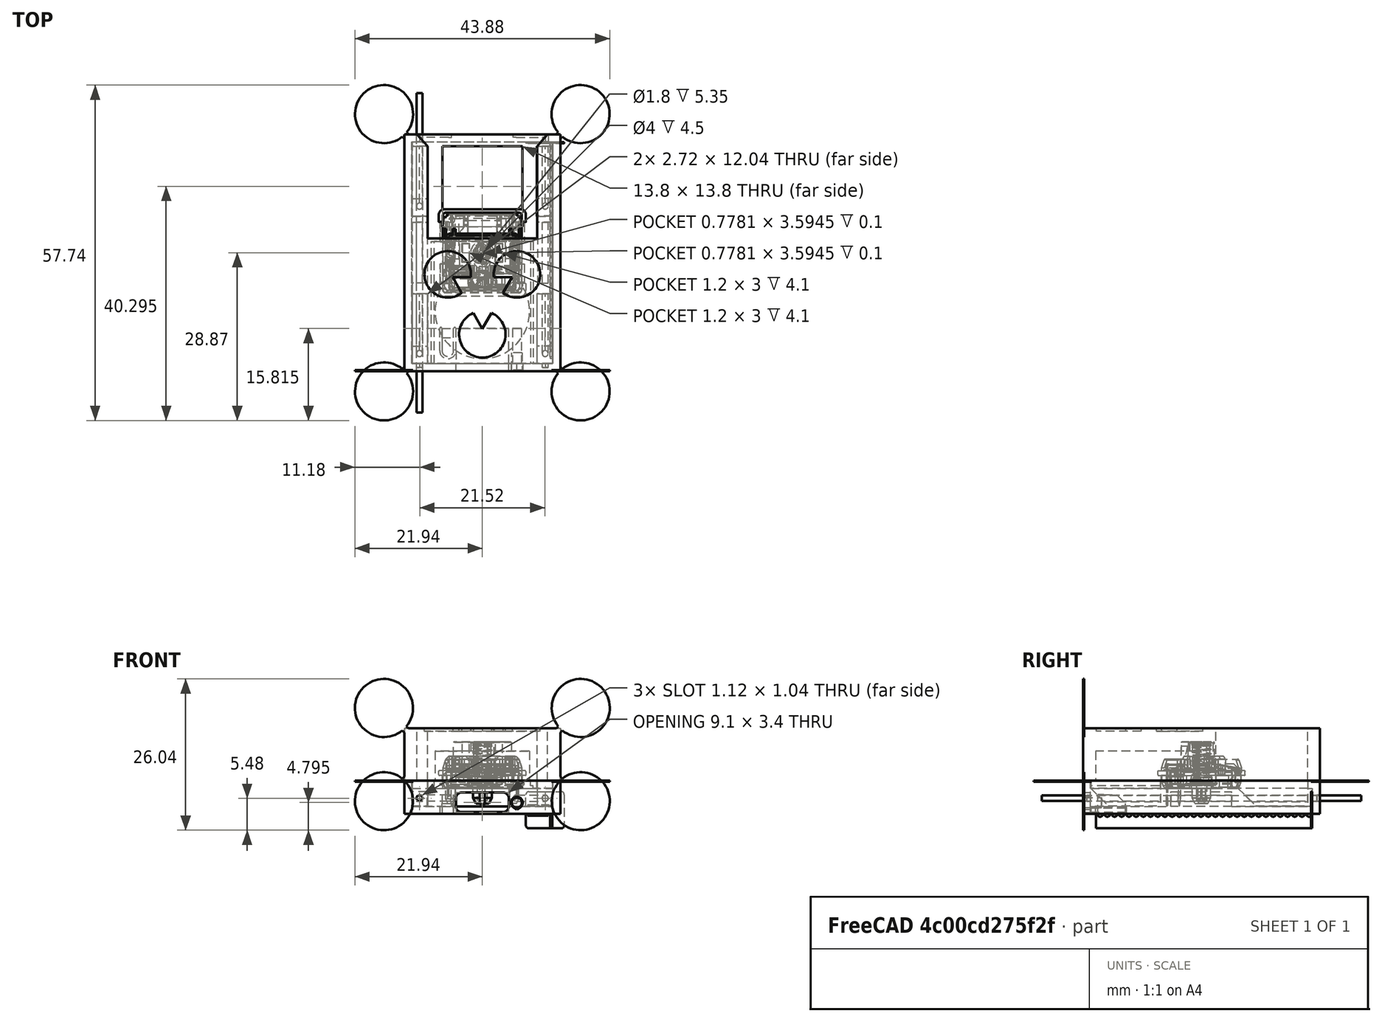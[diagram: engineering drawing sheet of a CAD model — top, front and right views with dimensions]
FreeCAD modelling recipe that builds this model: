
FCSTD DOCUMENT  (FreeCAD 1.1R42788 (Git))
Label: xiao_fit_2
License: All rights reserved
LicenseURL: https://en.wikipedia.org/wiki/All_rights_reserved
objects: Sketcher::SketchObject×31, PartDesign::Pocket×15, PartDesign::Pad×13, Part::Feature×8, App::Point×6, PartDesign::Mirrored×5, PartDesign::Body×5, PartDesign::Hole×3, App::VarSet×2, Mesh::Feature×2, App::Part×1, PartDesign::Chamfer×1, PartDesign::LinearPattern×1
note: 183 computed .brp shape members not serialized (recipe doc carries the construction recipe); baked Part::Feature solids carry a one-line shape summary decoded from their .brp

FEATURE [Sketcher::SketchObject] Sketch
  ArcFitTolerance = 1e-06
  AttachmentSupport = -> [XY_Plane]
  ExternalTypes = [0]
  FullyConstrained = true
  MakeInternals = false
  MapMode = 5
  expr: Constraints[20] = VarSet.ChocHoleWidth
  expr: Constraints[21] = VarSet.ChocHoleHeight
  expr: Constraints[32] = VarSet.XiaoHeight
  expr: Constraints[33] = VarSet.XiaoWidth
  expr: Constraints[34] = VarSet.WallThickness
  expr: Constraints[35] = 2 * VarSet.WallThickness
  expr: Constraints[48] = VarSet.KeycapFrameHorizontal
  expr: Constraints[49] = VarSet.KeycapHorizontalClearance
  expr: Constraints[50] = VarSet.KeycapVerticalClearance
  expr: Constraints[51] = VarSet.KeycapVerticalClearance
  sketch-geometry (20):
    g0: LineSegment StartX=-13.42 StartY=-20.375 StartZ=0 EndX=13.42 EndY=-20.375 EndZ=0
    g1: LineSegment StartX=13.42 StartY=-20.375 StartZ=0 EndX=13.42 EndY=20.375 EndZ=0
    g2: LineSegment StartX=13.42 StartY=20.375 StartZ=0 EndX=-13.42 EndY=20.375 EndZ=0
    g3: LineSegment StartX=-13.42 StartY=20.375 StartZ=0 EndX=-13.42 EndY=-20.375 EndZ=0
    g4: GeomPoint [constr] X=0 Y=0 Z=0
    g5: LineSegment StartX=-6.9 StartY=18.325 StartZ=0 EndX=-6.9 EndY=4.525 EndZ=0
    g6: LineSegment StartX=-6.9 StartY=4.525 StartZ=0 EndX=6.9 EndY=4.525 EndZ=0
    g7: LineSegment StartX=6.9 StartY=4.525 StartZ=0 EndX=6.9 EndY=18.325 EndZ=0
    g8: LineSegment StartX=6.9 StartY=18.325 StartZ=0 EndX=-6.9 EndY=18.325 EndZ=0
    g9: GeomPoint [constr] X=0 Y=11.425 Z=0
    g10: LineSegment StartX=-8.75 StartY=-19.075 StartZ=0 EndX=8.75 EndY=-19.075 EndZ=0
    g11: LineSegment StartX=8.75 StartY=-19.075 StartZ=0 EndX=8.75 EndY=1.925 EndZ=0
    g12: LineSegment StartX=8.75 StartY=1.925 StartZ=0 EndX=-8.75 EndY=1.925 EndZ=0
    g13: LineSegment StartX=-8.75 StartY=1.925 StartZ=0 EndX=-8.75 EndY=-19.075 EndZ=0
    g14: GeomPoint [constr] X=0 Y=-8.575 Z=0
    g15: LineSegment StartX=-13.42 StartY=20.375 StartZ=0 EndX=-9.42 EndY=20.375 EndZ=0
    g16: LineSegment StartX=-9.42 StartY=20.375 StartZ=0 EndX=-9.42 EndY=2.475 EndZ=0
    g17: LineSegment StartX=-9.42 StartY=2.475 StartZ=0 EndX=9.42 EndY=2.475 EndZ=0
    g18: LineSegment StartX=9.42 StartY=2.475 StartZ=0 EndX=9.42 EndY=20.375 EndZ=0
    g19: LineSegment StartX=9.42 StartY=20.375 StartZ=0 EndX=13.42 EndY=20.375 EndZ=0
  constraints (52):
    c: Coincident(g0,g1)
    c: Coincident(g1,g2)
    c: Coincident(g2,g3)
    c: Coincident(g3,g0)
    c: Horizontal(g0)
    c: Horizontal(g2)
    c: Vertical(g1)
    c: Vertical(g3)
    c: Symmetric(g2,g0,g4)
    c: Coincident(g4,g-1)
    c: Coincident(g5,g6)
    c: Coincident(g6,g7)
    c: Coincident(g7,g8)
    c: Coincident(g8,g5)
    c: Vertical(g5)
    c: Vertical(g7)
    c: Horizontal(g6)
    c: Horizontal(g8)
    c: Symmetric(g7,g5,g9)
    c: PointOnObject(g9,g-2)
    c: DistanceX(g8,g8) = 13.8
    c: DistanceY(g7,g7) = 13.8
    c: Coincident(g10,g11)
    c: Coincident(g11,g12)
    c: Coincident(g12,g13)
    c: Coincident(g13,g10)
    c: Horizontal(g10)
    c: Horizontal(g12)
    c: Vertical(g11)
    c: Vertical(g13)
    c: Symmetric(g12,g10,g14)
    c: PointOnObject(g14,g-2)
    c: DistanceY(g11,g11) = 21
    c: DistanceX(g12,g12) = 17.5
    c: DistanceY(g0,g10) = 1.3
    c: DistanceY(g12,g5) = 2.6
    c: Coincident(g2,g15)
    c: PointOnObject(g15,g2)
    c: Coincident(g15,g16)
    c: Vertical(g16)
    c: Coincident(g16,g17)
    c: Horizontal(g17)
    c: Coincident(g17,g18)
    c: PointOnObject(g18,g2)
    c: Vertical(g18)
    c: Coincident(g18,g19)
    c: Coincident(g19,g1)
    c: Equal(g15,g19)
    c: Distance(g19,g19) = 4
    c: DistanceX(g7,g18) = 2.52
    c: DistanceY(g17,g6) = 2.05
    c: DistanceY(g7,g18) = 2.05
FEATURE [App::VarSet] VarSet
  ChocBottomClearance = 5.7
  ChocHoleHeight = 13.8
  ChocHoleWidth = 13.8
  ChocHorizontalSpacing = 5
  ChocVerticalSpacing = 0.2
  Clearance = 0.02
  KeycapFrameHorizontal = 4
  KeycapHorizontalClearance = 2.52
  KeycapVerticalClearance = 2.05
  WallThickness = 1.3
  XiaoHeight = 21
  XiaoThickness = 1.25
  XiaoTopClearance = 0.5
  XiaoWidth = 17.5
  expr: ChocHoleHeight = 13.8 mm
FEATURE [PartDesign::Pad] Pad  label="Base"
  Direction = (0,0,1)
  Length = 1.3
  Length2 = 10
  Profile = -> Sketch [Edge3,Edge9,Edge1,Edge2]
  ReferenceAxis = -> Sketch [N_Axis]
  Refine = true
  Suppressed = false
  Type = 0
  expr: Length = VarSet.WallThickness
FEATURE [Sketcher::SketchObject] Sketch001
  ArcFitTolerance = 1e-06
  AttachmentSupport = -> [Pad]
  ExternalGeometry = -> [Sketch]
  ExternalTypes = [0]
  FullyConstrained = true
  MakeInternals = false
  MapMode = 5
  Placement = pos=(0,0,1.3) rot=(0,0,1;0rad)
  sketch-geometry (4):
    g0: LineSegment StartX=-6.9 StartY=18.325 StartZ=0 EndX=-6.9 EndY=4.525 EndZ=0
    g1: LineSegment StartX=-6.9 StartY=4.525 StartZ=0 EndX=6.9 EndY=4.525 EndZ=0
    g2: LineSegment StartX=6.9 StartY=4.525 StartZ=0 EndX=6.9 EndY=18.325 EndZ=0
    g3: LineSegment StartX=6.9 StartY=18.325 StartZ=0 EndX=-6.9 EndY=18.325 EndZ=0
  constraints (10):
    c: Coincident(g0,g1)
    c: Coincident(g1,g2)
    c: Coincident(g2,g3)
    c: Coincident(g3,g0)
    c: Vertical(g0)
    c: Vertical(g2)
    c: Horizontal(g1)
    c: Horizontal(g3)
    c: Coincident(g0,g-3)
    c: Coincident(g1,g-4)
FEATURE [PartDesign::Pocket] Pocket  label="ChocHole"
  BaseFeature = -> Pad
  Direction = (0,0,-1)
  Length = 5
  Length2 = 5
  Profile = -> Sketch001
  ReferenceAxis = -> Sketch001 [N_Axis]
  Refine = true
  Suppressed = false
  Type = 1
FEATURE [Mesh::Feature] MBK_Keycap___1u  label="MBK_Keycap_-_1u"
  Placement = pos=(0,0,6.61) rot=(0,0,1;0rad)
FEATURE [Part::Feature] Part__Feature  label="bottom_stabilizer"
  shape: bbox 15.16 x 15.16 x 5.85 mm, 308 faces (baked)
FEATURE [Part::Feature] Part__Feature001  label="contact"
  Placement = pos=(0,-5.9,0) rot=(0,0,1;0rad)
  shape: bbox 1.2 x 2.241 x 2.141 mm, 33 faces (baked)
FEATURE [Part::Feature] Part__Feature002  label="pin1"
  Placement = pos=(0,-5.9,0) rot=(0,0,1;0rad)
  shape: bbox 9.72 x 2.05 x 7 mm, 141 faces (baked)
FEATURE [Part::Feature] Part__Feature003  label="pin2"
  Placement = pos=(-5,-3.8,0) rot=(0,0,1;0rad)
  shape: bbox 3.2 x 0.65 x 7 mm, 30 faces (baked)
FEATURE [Part::Feature] Part__Feature004  label="top_stabilizer"
  Placement = pos=(0,0,3) rot=(0,0,1;0rad)
  shape: bbox 14.5 x 13.8 x 7.5 mm, 348 faces (baked)
FEATURE [Part::Feature] Part__Feature005  label="stabilizer"
  Placement = pos=(0,6.25,3) rot=(-1,0,0;0.20944rad)
  shape: bbox 9.432 x 7.756 x 2.155 mm, 7 faces (baked)
FEATURE [Part::Feature] Part__Feature006  label="stem_stabilizer"
  Placement = pos=(0,0,3.3) rot=(0,0,1;0rad)
  shape: bbox 11.5 x 5.7 x 7 mm, 99 faces (baked)
FEATURE [Part::Feature] Part__Feature007  label="shrunken_spring"
  Placement = pos=(0,0,4.15) rot=(0,0,1;0rad)
  shape: bbox 3.3 x 3.3 x 7.484 mm, 14 faces (baked)
FEATURE [App::Part] red  label="Choc"
  Group = -> [Part__Feature,Part__Feature001,Part__Feature002,Part__Feature003,Part__Feature004,Part__Feature005,Part__Feature006,Part__Feature007,MBK_Keycap___1u]
  Origin = -> Origin001
  Placement = pos=(0.08,11.69,-0.89) rot=(0,0,1;0rad)
  expr: .Placement.Base.z = 0
FEATURE [Mesh::Feature] SeeedXiao_01  label="SeeedXiao-01"
  Placement = pos=(-8.89,-20.59,0.4) rot=(0.707107,0.707107,0;3.14159rad)
FEATURE [Sketcher::SketchObject] Sketch002
  ArcFitTolerance = 1e-06
  AttachmentSupport = -> [Pocket]
  ExternalGeometry = -> [Pocket]
  ExternalTypes = [0]
  FullyConstrained = true
  MakeInternals = false
  MapMode = 5
  Placement = pos=(0,0,0) rot=(1,0,0;3.14159rad)
  expr: Constraints[18] = VarSet.WallThickness
  expr: Constraints[19] = VarSet.WallThickness
  expr: Constraints[20] = VarSet.WallThickness
  expr: Constraints[21] = VarSet.WallThickness
  sketch-geometry (8):
    g0: LineSegment StartX=-13.42 StartY=20.375 StartZ=0 EndX=-13.42 EndY=-20.375 EndZ=0
    g1: LineSegment StartX=-13.42 StartY=-20.375 StartZ=0 EndX=13.42 EndY=-20.375 EndZ=0
    g2: LineSegment StartX=13.42 StartY=-20.375 StartZ=0 EndX=13.42 EndY=20.375 EndZ=0
    g3: LineSegment StartX=13.42 StartY=20.375 StartZ=0 EndX=-13.42 EndY=20.375 EndZ=0
    g4: LineSegment StartX=-12.12 StartY=19.075 StartZ=0 EndX=-12.12 EndY=-19.075 EndZ=0
    g5: LineSegment StartX=-12.12 StartY=-19.075 StartZ=0 EndX=12.12 EndY=-19.075 EndZ=0
    g6: LineSegment StartX=12.12 StartY=-19.075 StartZ=0 EndX=12.12 EndY=19.075 EndZ=0
    g7: LineSegment StartX=12.12 StartY=19.075 StartZ=0 EndX=-12.12 EndY=19.075 EndZ=0
  constraints (22):
    c: Coincident(g0,g1)
    c: Coincident(g1,g2)
    c: Coincident(g2,g3)
    c: Coincident(g3,g0)
    c: Vertical(g0)
    c: Vertical(g2)
    c: Horizontal(g1)
    c: Horizontal(g3)
    c: Coincident(g0,g-3)
    c: Coincident(g1,g-4)
    c: Coincident(g4,g5)
    c: Coincident(g5,g6)
    c: Coincident(g6,g7)
    c: Coincident(g7,g4)
    c: Vertical(g4)
    c: Vertical(g6)
    c: Horizontal(g5)
    c: Horizontal(g7)
    c: DistanceX(g6,g2) = 1.3
    c: DistanceX(g0,g4) = 1.3
    c: DistanceY(g6,g2) = 1.3
    c: DistanceY(g1,g5) = 1.3
FEATURE [PartDesign::Pad] Pad001  label="Walls"
  BaseFeature = -> Pocket
  Direction = (0,0,-1)
  Length = 4.4
  Length2 = 10
  Profile = -> Sketch002
  ReferenceAxis = -> Sketch002 [N_Axis]
  Refine = true
  Suppressed = false
  Type = 0
  expr: Length = VarSet.ChocBottomClearance - VarSet.WallThickness
FEATURE [Sketcher::SketchObject] Sketch003
  ArcFitTolerance = 1e-06
  AttachmentSupport = -> [Pad001]
  ExternalGeometry = -> [Sketch]
  ExternalTypes = [0]
  FullyConstrained = true
  MakeInternals = false
  MapMode = 5
  Placement = pos=(0,0,0) rot=(1,0,0;3.14159rad)
  expr: Constraints[5] = VarSet.Clearance
  expr: Constraints[7] = VarSet.Clearance
  expr: Constraints[8] = VarSet.Clearance
  sketch-geometry (4):
    g0: LineSegment StartX=-8.77 StartY=19.075 StartZ=0 EndX=-8.77 EndY=-1.945 EndZ=0
    g1: LineSegment StartX=-8.77 StartY=-1.945 StartZ=0 EndX=8.77 EndY=-1.945 EndZ=0
    g2: LineSegment StartX=8.77 StartY=-1.945 StartZ=0 EndX=8.77 EndY=19.075 EndZ=0
    g3: LineSegment StartX=8.77 StartY=19.075 StartZ=0 EndX=-8.77 EndY=19.075 EndZ=0
  constraints (12):
    c: Coincident(g0,g1)
    c: Coincident(g1,g2)
    c: Vertical(g0)
    c: Vertical(g2)
    c: Horizontal(g1)
    c: DistanceX(g0,g-3) = 0.02
    c: Horizontal(g2,g-4)
    c: DistanceX(g-4,g2) = 0.02
    c: DistanceY(g1,g-4) = 0.02
    c: Coincident(g3,g2)
    c: Coincident(g3,g0)
    c: Horizontal(g3)
FEATURE [PartDesign::Pocket] Pocket001  label="XiaoHole"
  BaseFeature = -> Pad001
  Direction = (0,0,1)
  Length = 0.4
  Length2 = 5
  Profile = -> Sketch003
  ReferenceAxis = -> Sketch003 [N_Axis]
  Refine = true
  Suppressed = false
  Type = 0
FEATURE [Sketcher::SketchObject] Sketch004
  ArcFitTolerance = 1e-06
  AttachmentSupport = -> [Pocket001]
  ExternalGeometry = -> [Pocket001]
  ExternalTypes = [0]
  FullyConstrained = true
  MakeInternals = false
  MapMode = 5
  Placement = pos=(0,0,0.4) rot=(1,0,0;3.14159rad)
  sketch-geometry (4):
    g0: LineSegment StartX=-8.27 StartY=19.075 StartZ=0 EndX=-8.27 EndY=-1.945 EndZ=0
    g1: LineSegment StartX=-8.27 StartY=-1.945 StartZ=0 EndX=8.27 EndY=-1.945 EndZ=0
    g2: LineSegment StartX=8.27 StartY=-1.945 StartZ=0 EndX=8.27 EndY=19.075 EndZ=0
    g3: LineSegment StartX=8.27 StartY=19.075 StartZ=0 EndX=-8.27 EndY=19.075 EndZ=0
  constraints (12):
    c: Coincident(g0,g1)
    c: Coincident(g1,g2)
    c: Coincident(g2,g3)
    c: Coincident(g3,g0)
    c: Vertical(g0)
    c: Vertical(g2)
    c: Horizontal(g1)
    c: Horizontal(g3)
    c: PointOnObject(g0,g-5)
    c: PointOnObject(g1,g-6)
    c: DistanceX(g1,g-6) = 0.5
    c: DistanceX(g-6,g0) = 0.5
FEATURE [PartDesign::Pocket] Pocket002  label="XiaoHolder"
  BaseFeature = -> Pocket001
  Direction = (0,0,1)
  Length = 5
  Length2 = 5
  Profile = -> Sketch004
  ReferenceAxis = -> Sketch004 [N_Axis]
  Refine = true
  Suppressed = false
  Type = 0
FEATURE [Sketcher::SketchObject] Sketch005
  ArcFitTolerance = 1e-06
  AttachmentSupport = -> [Pocket002]
  ExternalGeometry = -> [Pocket002]
  ExternalTypes = [0]
  FullyConstrained = true
  MakeInternals = false
  MapMode = 5
  Placement = pos=(0,-20.375,1.2e-14) rot=(1,0,0;1.5708rad)
  sketch-geometry (13):
    g0: LineSegment StartX=-3.55 StartY=-4.125 StartZ=0 EndX=3.55 EndY=-4.125 EndZ=0
    g1: LineSegment StartX=4.55 StartY=-3.125 StartZ=0 EndX=4.55 EndY=-1.725 EndZ=0
    g2: LineSegment StartX=3.55 StartY=-0.725 StartZ=0 EndX=-3.55 EndY=-0.725 EndZ=0
    g3: LineSegment StartX=-4.55 StartY=-1.725 StartZ=0 EndX=-4.55 EndY=-3.125 EndZ=0
    g4: ArcOfCircle CenterX=-3.55 CenterY=-3.125 CenterZ=0 NormalX=0 NormalY=0 NormalZ=1 AngleXU=0 Radius=1 StartAngle=3.14159 EndAngle=4.71239
    g5: ArcOfCircle CenterX=3.55 CenterY=-3.125 CenterZ=0 NormalX=0 NormalY=0 NormalZ=1 AngleXU=0 Radius=1 StartAngle=4.71239 EndAngle=6.28319
    g6: ArcOfCircle CenterX=3.55 CenterY=-1.725 CenterZ=0 NormalX=0 NormalY=0 NormalZ=1 AngleXU=0 Radius=1 StartAngle=0 EndAngle=1.5708
    g7: ArcOfCircle CenterX=-3.55 CenterY=-1.725 CenterZ=0 NormalX=0 NormalY=0 NormalZ=1 AngleXU=0 Radius=1 StartAngle=1.5708 EndAngle=3.14159
    g8: GeomPoint [constr] X=-4.55 Y=-4.125 Z=0
    g9: GeomPoint [constr] X=4.55 Y=-0.725 Z=0
    g10: ArcOfCircle CenterX=5.95 CenterY=-2.475 CenterZ=0 NormalX=0 NormalY=0 NormalZ=1 AngleXU=0 Radius=1 StartAngle=5.23599 EndAngle=10.472
    g11: LineSegment StartX=5.95 StartY=-3.6297 StartZ=0 EndX=5.45 EndY=-3.34103 EndZ=0
    g12: LineSegment StartX=5.95 StartY=-3.6297 StartZ=0 EndX=6.45 EndY=-3.34103 EndZ=0
  constraints (31):
    c: Tangent(g0,g4) = -1.5708
    c: Tangent(g0,g5) = -1.5708
    c: Tangent(g1,g5) = -1.5708
    c: Tangent(g1,g6) = -1.5708
    c: Tangent(g2,g6) = -1.5708
    c: Tangent(g2,g7) = -1.5708
    c: Tangent(g3,g7) = -1.5708
    c: Tangent(g3,g4) = -1.5708
    c: Horizontal(g0)
    c: Vertical(g1)
    c: Vertical(g3)
    c: Equal(g4,g5)
    c: Equal(g5,g6)
    c: Equal(g6,g7)
    c: PointOnObject(g8,g0)
    c: PointOnObject(g8,g3)
    c: PointOnObject(g9,g1)
    c: PointOnObject(g9,g2)
    c: Radius(g5) = 1
    c: DistanceX(g3,g1) = 9.1
    c: DistanceY(g0,g2) = 3.4
    c: Symmetric(g2,g2,g-2)
    c: DistanceY(g2,g-4) = 1.125
    c: DistanceX(g1,g10) = 1.4
    c: DistanceY(g10,g1) = 0.75
    c: Coincident(g12,g11)
    c: Angle(g12,g11) = 2.0944
    c: Horizontal(g12,g11)
    c: Diameter(g10) = 2
    c: Tangent(g11,g10) = 1.5708
    c: Tangent(g12,g10) = -1.5708
FEATURE [PartDesign::Pocket] Pocket003  label="USB-Hole"
  BaseFeature = -> Pocket002
  Direction = (0,1,-2e-16)
  Length = 5
  Length2 = 5
  Profile = -> Sketch005
  ReferenceAxis = -> Sketch005 [N_Axis]
  Refine = true
  Suppressed = false
  Type = 2
FEATURE [App::Point] Origin004  label="Origin"
  Role = Origin
FEATURE [App::Point] Origin005  label="Origin"
  Role = Origin
FEATURE [Sketcher::SketchObject] Sketch010
  ArcFitTolerance = 1e-06
  AttachmentSupport = -> [Pad001]
  ExternalGeometry = -> [Pocket003]
  ExternalTypes = [0,0,0]
  FullyConstrained = true
  MakeInternals = false
  MapMode = 5
  Placement = pos=(0,20.375,-1.2e-14) rot=(0,0.707107,0.707107;3.14159rad)
  sketch-geometry (1):
    g0: Circle CenterX=-10.82 CenterY=-1.7 CenterZ=0 NormalX=0 NormalY=0 NormalZ=1 AngleXU=0 Radius=0.5
  constraints (3):
    c: Diameter(g0) = 1
    c: DistanceY(g-4,g0) = 2.7
    c: DistanceX(g-4,g0) = 1.3
FEATURE [PartDesign::Hole] Hole  label="PinHole"
  BaseFeature = -> Pocket003
  BaseProfileType = 7
  CustomThreadClearance = 0
  Depth = 5
  DepthType = 0
  Diameter = 1.04
  DrillForDepth = false
  DrillPoint = 1
  DrillPointAngle = 118
  HoleCutCountersinkAngle = 90
  HoleCutCustomValues = false
  HoleCutDepth = 0
  HoleCutDiameter = 0
  HoleCutType = 0
  ModelThread = false
  Profile = -> Sketch010
  Refine = true
  Suppressed = false
  Tapered = false
  TaperedAngle = 90
  TeardropAngle = 120
  TeardropRotation = 270
  ThreadClass = 0
  ThreadDepth = 5
  ThreadDepthType = 0
  ThreadDiameter = 1.04
  ThreadDirection = 0
  ThreadFit = 0
  ThreadSize = 0
  ThreadType = 0
  Threaded = false
  UseCustomThreadClearance = false
  expr: Diameter = 1 mm + 2 * VarSet.Clearance
FEATURE [Sketcher::SketchObject] Sketch010_Teardrops
  ArcFitTolerance = 1e-06
  AttachmentSupport = -> [Sketch010]
  ExternalTypes = [0]
  FullyConstrained = true
  MakeInternals = false
  MapMode = 2
  Placement = pos=(0,20.375,-1.2e-14) rot=(0,0.707107,0.707107;3.14159rad)
  expr: Constraints[5] = Sketch010.Geometry[0].Center.x * 1 mm
  expr: Constraints[6] = Sketch010.Geometry[0].Center.y * 1 mm
  expr: Constraints[7] = Hole.Diameter
  expr: Constraints[8] = Hole.TeardropAngle
  expr: Constraints[9] = Hole.TeardropRotation
  sketch-geometry (4):
    g0: ArcOfCircle CenterX=-10.82 CenterY=-1.7 CenterZ=0 NormalX=0 NormalY=0 NormalZ=1 AngleXU=0 Radius=0.52 StartAngle=5.23599 EndAngle=10.472
    g1: LineSegment StartX=-10.56 StartY=-2.15033 StartZ=0 EndX=-10.82 EndY=-2.30044 EndZ=0
    g2: LineSegment StartX=-11.08 StartY=-2.15033 StartZ=0 EndX=-10.82 EndY=-2.30044 EndZ=0
    g3: LineSegment [constr] StartX=-10.82 StartY=-1.7 StartZ=0 EndX=-10.82 EndY=-2.30044 EndZ=0
  constraints (10):
    c: Coincident(g1,g2)
    c: Coincident(g1,g3)
    c: Coincident(g0,g3)
    c: Tangent(g0,g1) = 1.5708
    c: Tangent(g0,g2) = -1.5708
    c: DistanceX(g0) = -10.82
    c: DistanceY(g0) = -1.7
    c: Diameter(g0) = 1.04
    c: Angle(g1,g2) = 2.0944
    c: Angle(g3) = 4.71239
FEATURE [PartDesign::Pocket] Hole_Teardrops  label="PinHole_Teardrops"
  BaseFeature = -> Hole
  Direction = (0,-1,2e-16)
  Length = 5
  Length2 = 5
  Profile = -> Sketch010_Teardrops
  ReferenceAxis = -> Sketch010_Teardrops [N_Axis]
  Refine = true
  Suppressed = false
  Type = 0
  expr: Length = Hole.Depth
  expr: Type = Hole.DepthType
FEATURE [App::Point] Origin008
  Role = Origin
FEATURE [Sketcher::SketchObject] Sketch016
  ArcFitTolerance = 1e-06
  AttachmentSupport = -> [Origin007]
  ExternalTypes = [0]
  FullyConstrained = true
  MakeInternals = false
  MapMode = 5
  expr: Constraints[6] = VarSet.ChocHoleWidth + 2 * VarSet.KeycapHorizontalClearance + 2 * VarSet.KeycapFrameHorizontal - 2 * VarSet.WallThickness - 2 * VarSet.Clearance
  expr: Constraints[8] = VarSet.KeycapVerticalClearance + VarSet.ChocHoleHeight + VarSet.WallThickness + VarSet.XiaoHeight - 2 * VarSet.Clearance
  sketch-geometry (4):
    g0: LineSegment StartX=-12.1 StartY=19.055 StartZ=0 EndX=-12.1 EndY=-19.055 EndZ=0
    g1: LineSegment StartX=-12.1 StartY=-19.055 StartZ=0 EndX=12.1 EndY=-19.055 EndZ=0
    g2: LineSegment StartX=12.1 StartY=-19.055 StartZ=0 EndX=12.1 EndY=19.055 EndZ=0
    g3: LineSegment StartX=12.1 StartY=19.055 StartZ=0 EndX=-12.1 EndY=19.055 EndZ=0
  constraints (10):
    c: Coincident(g0,g1)
    c: Coincident(g1,g2)
    c: Coincident(g2,g3)
    c: Coincident(g3,g0)
    c: Vertical(g0)
    c: Horizontal(g1)
    c: DistanceX(g3,g3) = 24.2
    c: Symmetric(g2,g0,g-2)
    c: DistanceY(g2,g2) = 38.11
    c: Symmetric(g2,g1,g-1)
FEATURE [PartDesign::Pad] Pad004  label="Body001"
  Direction = (0,0,1)
  Length = 1.3
  Length2 = 10
  Profile = -> Sketch016
  ReferenceAxis = -> Sketch016 [N_Axis]
  Refine = true
  Suppressed = false
  Type = 0
  expr: Length = VarSet.WallThickness
FEATURE [Sketcher::SketchObject] Sketch017
  ArcFitTolerance = 1e-06
  AttachmentSupport = -> [Pad004]
  ExternalTypes = [0]
  FullyConstrained = false
  MakeInternals = false
  MapMode = 5
  Placement = pos=(0,-19.055,0) rot=(1,0,0;1.5708rad)
  sketch-geometry (11):
    g0: LineSegment StartX=-4.55 StartY=2.69281 StartZ=0 EndX=-4.55 EndY=1.29281 EndZ=0
    g1: LineSegment StartX=-3.55 StartY=0.292812 StartZ=0 EndX=3.55 EndY=0.292812 EndZ=0
    g2: LineSegment StartX=4.55 StartY=1.29281 StartZ=0 EndX=4.55 EndY=2.69281 EndZ=0
    g3: LineSegment StartX=3.55 StartY=3.69281 StartZ=0 EndX=-3.55 EndY=3.69281 EndZ=0
    g4: ArcOfCircle CenterX=-3.55 CenterY=2.69281 CenterZ=0 NormalX=0 NormalY=0 NormalZ=1 AngleXU=0 Radius=1 StartAngle=1.5708 EndAngle=3.14159
    g5: ArcOfCircle CenterX=-3.55 CenterY=1.29281 CenterZ=0 NormalX=0 NormalY=0 NormalZ=1 AngleXU=0 Radius=1 StartAngle=3.14159 EndAngle=4.71239
    g6: ArcOfCircle CenterX=3.55 CenterY=1.29281 CenterZ=0 NormalX=0 NormalY=0 NormalZ=1 AngleXU=0 Radius=1 StartAngle=4.71239 EndAngle=6.28319
    g7: ArcOfCircle CenterX=3.55 CenterY=2.69281 CenterZ=0 NormalX=0 NormalY=0 NormalZ=1 AngleXU=0 Radius=1 StartAngle=0 EndAngle=1.5708
    g8: GeomPoint [constr] X=-4.55 Y=3.69281 Z=0
    g9: GeomPoint [constr] X=4.55 Y=0.292812 Z=0
    g10: Circle CenterX=5.95 CenterY=1.94281 CenterZ=0 NormalX=0 NormalY=0 NormalZ=1 AngleXU=0 Radius=1
  constraints (25):
    c: Tangent(g0,g4) = -1.5708
    c: Tangent(g0,g5) = -1.5708
    c: Tangent(g1,g5) = -1.5708
    c: Tangent(g1,g6) = -1.5708
    c: Tangent(g2,g6) = -1.5708
    c: Tangent(g2,g7) = -1.5708
    c: Tangent(g3,g7) = -1.5708
    c: Tangent(g3,g4) = -1.5708
    c: Vertical(g0)
    c: Vertical(g2)
    c: Horizontal(g1)
    c: Equal(g4,g5)
    c: Equal(g5,g6)
    c: Equal(g6,g7)
    c: PointOnObject(g8,g0)
    c: PointOnObject(g8,g3)
    c: PointOnObject(g9,g1)
    c: PointOnObject(g9,g2)
    c: Radius(g5) = 1
    c: DistanceX(g0,g2) = 9.1
    c: DistanceY(g1,g3) = 3.4
    c: Symmetric(g3,g3,g-2)
    c: DistanceX(g2,g10) = 1.4
    c: Diameter(g10) = 2
    c: DistanceY(g10,g2) = 0.75
FEATURE [PartDesign::Pocket] Pocket007  label="USB-Hole001"
  BaseFeature = -> Pad004
  Direction = (0,1,-2e-16)
  Length = 6
  Length2 = 5
  Profile = -> Sketch017
  ReferenceAxis = -> Sketch017 [N_Axis]
  Refine = true
  Suppressed = false
  Type = 0
FEATURE [Sketcher::SketchObject] Sketch018
  ArcFitTolerance = 1e-06
  AttachmentSupport = -> [Pocket007]
  ExternalGeometry = -> [Pocket007]
  ExternalTypes = [0,0]
  FullyConstrained = false
  MakeInternals = false
  MapMode = 5
  Placement = pos=(0,0,1.3) rot=(0,0,1;0rad)
  sketch-geometry (8):
    g0: LineSegment StartX=-4.55 StartY=-13.055 StartZ=0 EndX=-4.55 EndY=-16.8372 EndZ=0
    g1: LineSegment StartX=-7.35 StartY=-16.8372 StartZ=0 EndX=-7.35 EndY=-13.055 EndZ=0
    g2: ArcOfCircle CenterX=-7.15 CenterY=-13.055 CenterZ=0 NormalX=0 NormalY=0 NormalZ=1 AngleXU=0 Radius=0.2 StartAngle=2.5e-15 EndAngle=3.14159
    g3: LineSegment StartX=-6.95 StartY=-13.055 StartZ=0 EndX=-6.95 EndY=-16.8372 EndZ=0
    g4: LineSegment StartX=-4.95 StartY=-16.8372 StartZ=0 EndX=-4.95 EndY=-13.055 EndZ=0
    g5: ArcOfCircle CenterX=-4.75 CenterY=-13.055 CenterZ=0 NormalX=0 NormalY=0 NormalZ=1 AngleXU=0 Radius=0.2 StartAngle=3.6269e-08 EndAngle=3.14159
    g6: ArcOfCircle CenterX=-5.95 CenterY=-16.8372 CenterZ=0 NormalX=0 NormalY=0 NormalZ=1 AngleXU=0 Radius=1 StartAngle=3.14159 EndAngle=6.28319
    g7: ArcOfCircle CenterX=-5.95 CenterY=-16.8372 CenterZ=0 NormalX=0 NormalY=0 NormalZ=1 AngleXU=0 Radius=1.4 StartAngle=3.14159 EndAngle=6.28319
  constraints (18):
    c: Vertical(g0)
    c: Vertical(g1)
    c: Tangent(g1,g2) = 1.5708
    c: Tangent(g2,g3) = 1.5708
    c: Tangent(g4,g5) = 1.5708
    c: Coincident(g5,g0)
    c: Equal(g5,g2)
    c: Radius(g5) = 0.2
    c: Vertical(g3)
    c: Vertical(g4)
    c: Equal(g3,g4)
    c: Coincident(g7,g6)
    c: Tangent(g6,g4) = -1.5708
    c: Tangent(g6,g3) = -1.5708
    c: DistanceX(g2,g4) = 2
    c: Coincident(g0,g-3)
    c: Tangent(g7,g1) = 1.5708
    c: Tangent(g7,g0) = 1.5708
FEATURE [Sketcher::SketchObject] Sketch019
  ArcFitTolerance = 1e-06
  AttachmentSupport = -> [Pad004]
  ExternalGeometry = -> [Pad004]
  ExternalTypes = [0]
  FullyConstrained = false
  MakeInternals = false
  MapMode = 5
  Placement = pos=(0,0,1.3) rot=(0,0,1;0rad)
  sketch-geometry (4):
    g0: LineSegment StartX=12.1 StartY=5.24157 StartZ=0 EndX=9.5 EndY=5.24157 EndZ=0
    g1: LineSegment StartX=9.5 StartY=5.24157 StartZ=0 EndX=9.5 EndY=-5.24157 EndZ=0
    g2: LineSegment StartX=9.5 StartY=-5.24157 StartZ=0 EndX=12.1 EndY=-5.24157 EndZ=0
    g3: LineSegment StartX=12.1 StartY=-5.24157 StartZ=0 EndX=12.1 EndY=5.24157 EndZ=0
  constraints (10):
    c: Coincident(g0,g1)
    c: Coincident(g1,g2)
    c: Coincident(g2,g3)
    c: Coincident(g3,g0)
    c: Horizontal(g0)
    c: Horizontal(g2)
    c: Vertical(g3)
    c: Symmetric(g0,g1,g-1)
    c: DistanceX(g0,g0) = 2.6
    c: PointOnObject(g0,g-3)
FEATURE [PartDesign::Pad] Pad005  label="Holder"
  BaseFeature = -> Pocket007
  Direction = (0,0,1)
  Length = 2.5
  Length2 = 10
  Profile = -> Sketch019
  ReferenceAxis = -> Sketch019 [N_Axis]
  Refine = true
  Suppressed = false
  Type = 0
FEATURE [Sketcher::SketchObject] Sketch020
  ArcFitTolerance = 1e-06
  AttachmentSupport = -> [Pad005]
  ExternalGeometry = -> [Pad005]
  ExternalTypes = [0,0]
  FullyConstrained = true
  MakeInternals = false
  MapMode = 5
  Placement = pos=(0,-5.24157,0) rot=(1,0,0;1.5708rad)
  expr: Constraints[1] = 1.3 mm - VarSet.Clearance
  sketch-geometry (1):
    g0: Circle CenterX=10.82 CenterY=2.7 CenterZ=0 NormalX=0 NormalY=0 NormalZ=1 AngleXU=0 Radius=0.5
  constraints (3):
    c: Diameter(g0) = 1
    c: DistanceX(g0,g-3) = 1.28
    c: DistanceY(g-1,g0) = 2.7
FEATURE [PartDesign::Hole] Hole002  label="PinHole001"
  BaseFeature = -> Pad005
  BaseProfileType = 7
  CustomThreadClearance = 0
  Depth = 25
  DepthType = 0
  Diameter = 1.04
  DrillForDepth = false
  DrillPoint = 1
  DrillPointAngle = 118
  HoleCutCountersinkAngle = 90
  HoleCutCustomValues = false
  HoleCutDepth = 0
  HoleCutDiameter = 0
  HoleCutType = 0
  ModelThread = false
  Profile = -> Sketch020
  Refine = true
  Suppressed = false
  Tapered = false
  TaperedAngle = 90
  TeardropAngle = 120
  TeardropRotation = 90
  ThreadClass = 0
  ThreadDepth = 25
  ThreadDepthType = 0
  ThreadDiameter = 1.04
  ThreadDirection = 0
  ThreadFit = 0
  ThreadSize = 0
  ThreadType = 0
  Threaded = false
  UseCustomThreadClearance = false
  expr: Diameter = 1 mm + 2 * VarSet.Clearance
FEATURE [PartDesign::Mirrored] Mirrored002  label="Second Holder"
  BaseFeature = -> Hole002
  MirrorPlane = -> Sketch019 [V_Axis]
  Originals = -> [Pad005,Hole002]
  Refine = true
  Suppressed = false
  TransformMode = 0
FEATURE [PartDesign::Pocket] Pocket008  label="Reset Lever"
  BaseFeature = -> Mirrored002
  Direction = (0,0,-1)
  Length = 5
  Length2 = 5
  Profile = -> Sketch018
  ReferenceAxis = -> Sketch018 [N_Axis]
  Refine = true
  Suppressed = false
  Type = 1
FEATURE [Sketcher::SketchObject] Sketch021
  ArcFitTolerance = 1e-06
  AttachmentSupport = -> [Mirrored002]
  ExternalGeometry = -> [Pocket008]
  ExternalTypes = [0,0,0]
  FullyConstrained = true
  MakeInternals = false
  MapMode = 5
  Placement = pos=(0,0,1.3) rot=(0,0,1;0rad)
  sketch-geometry (1):
    g0: LineSegment StartX=-6.95 StartY=-13.055 StartZ=0 EndX=-4.95 EndY=-13.055 EndZ=0
  constraints (2):
    c: Coincident(g0,g-3)
    c: Coincident(g0,g-4)
FEATURE [PartDesign::Pad] Pad006  label="Reset Button"
  BaseFeature = -> Pocket008
  Direction = (0,0,1)
  Length = 2
  Length2 = 10
  Profile = -> Sketch021
  ReferenceAxis = -> Sketch021 [N_Axis]
  Refine = true
  Suppressed = false
  Type = 0
FEATURE [App::Point] Origin010
  Role = Origin
FEATURE [Sketcher::SketchObject] Sketch022
  ArcFitTolerance = 1e-06
  AttachmentSupport = -> [Origin009]
  ExternalTypes = [0]
  FullyConstrained = false
  MakeInternals = false
  MapMode = 5
  expr: Constraints[31] = VarSet.ChocHoleWidth + 2 * VarSet.KeycapHorizontalClearance
  expr: Constraints[32] = VarSet.KeycapVerticalClearance
  expr: Constraints[33] = VarSet.ChocHoleWidth + VarSet.KeycapVerticalClearance
  expr: Constraints[6] = VarSet001.ChocHoleWidth + 2 * VarSet001.KeycapHorizontalClearance + 2 * VarSet001.KeycapFrameHorizontal
  expr: Constraints[8] = VarSet001.KeycapVerticalClearance + VarSet001.ChocHoleHeight + 3 * VarSet001.WallThickness + VarSet001.XiaoHeight
  sketch-geometry (14):
    g0: LineSegment [constr] StartX=-13.42 StartY=20.375 StartZ=0 EndX=-13.42 EndY=-20.375 EndZ=0
    g1: LineSegment [constr] StartX=-13.42 StartY=-20.375 StartZ=0 EndX=13.42 EndY=-20.375 EndZ=0
    g2: LineSegment [constr] StartX=13.42 StartY=-20.375 StartZ=0 EndX=13.42 EndY=20.375 EndZ=0
    g3: LineSegment [constr] StartX=13.42 StartY=20.375 StartZ=0 EndX=-13.42 EndY=20.375 EndZ=0
    g4: LineSegment StartX=-11.247 StartY=20.375 StartZ=0 EndX=-9.42 EndY=18.325 EndZ=0
    g5: LineSegment StartX=-9.42 StartY=18.325 StartZ=0 EndX=-9.42 EndY=2.475 EndZ=0
    g6: LineSegment StartX=-9.42 StartY=2.475 StartZ=0 EndX=9.42 EndY=2.475 EndZ=0
    g7: LineSegment StartX=9.42 StartY=2.475 StartZ=0 EndX=9.42 EndY=18.325 EndZ=0
    g8: LineSegment StartX=9.42 StartY=18.325 StartZ=0 EndX=11.247 EndY=20.375 EndZ=0
    g9: LineSegment StartX=11.247 StartY=20.375 StartZ=0 EndX=13.42 EndY=20.375 EndZ=0
    g10: LineSegment StartX=13.42 StartY=20.375 StartZ=0 EndX=13.42 EndY=-20.375 EndZ=0
    g11: LineSegment StartX=13.42 StartY=-20.375 StartZ=0 EndX=-13.42 EndY=-20.375 EndZ=0
    g12: LineSegment StartX=-13.42 StartY=-20.375 StartZ=0 EndX=-13.42 EndY=20.375 EndZ=0
    g13: LineSegment StartX=-13.42 StartY=20.375 StartZ=0 EndX=-11.247 EndY=20.375 EndZ=0
  constraints (34):
    c: Coincident(g0,g1)
    c: Coincident(g1,g2)
    c: Coincident(g2,g3)
    c: Coincident(g3,g0)
    c: Vertical(g0)
    c: Horizontal(g1)
    c: DistanceX(g3,g3) = 26.84
    c: Symmetric(g2,g0,g-2)
    c: DistanceY(g2,g2) = 40.75
    c: Symmetric(g2,g1,g-1)
    c: PointOnObject(g4,g3)
    c: Coincident(g4,g5)
    c: Vertical(g5)
    c: Coincident(g5,g6)
    c: Coincident(g6,g7)
    c: Vertical(g7)
    c: Coincident(g7,g8)
    c: PointOnObject(g8,g3)
    c: Coincident(g8,g9)
    c: Coincident(g9,g2)
    c: Coincident(g9,g10)
    c: Coincident(g10,g1)
    c: Coincident(g10,g11)
    c: Coincident(g11,g0)
    c: Coincident(g11,g12)
    c: Coincident(g12,g0)
    c: Coincident(g12,g13)
    c: Coincident(g13,g4)
    c: Equal(g8,g4)
    c: Equal(g7,g5)
    c: Symmetric(g6,g5,g-2)
    c: DistanceX(g6,g6) = 18.84
    c: DistanceY(g7,g2) = 2.05
    c: DistanceY(g7,g7) = 15.85
FEATURE [App::VarSet] VarSet001
  ChocBottomClearance = 5.7
  ChocHoleHeight = 13.8
  ChocHoleWidth = 13.8
  ChocHorizontalSpacing = 5
  ChocVerticalSpacing = 0.2
  Clearance = 0.02
  KeycapFrameHorizontal = 4
  KeycapHorizontalClearance = 2.52
  KeycapVerticalClearance = 2.05
  WallThickness = 1.3
  XiaoHeight = 21
  XiaoThickness = 1.25
  XiaoTopClearance = 0.5
  XiaoWidth = 17.5
  expr: ChocHoleHeight = 13.8 mm
FEATURE [PartDesign::Pad] Pad007
  Direction = (0,0,1)
  Length = 9
  Length2 = 10
  Profile = -> Sketch022
  ReferenceAxis = -> Sketch022 [N_Axis]
  Refine = true
  Suppressed = false
  Type = 0
FEATURE [Sketcher::SketchObject] Sketch023
  ArcFitTolerance = 1e-06
  AttachmentSupport = -> [Pad007]
  ExternalGeometry = -> [Pad007]
  ExternalTypes = [0,0,0,0,0]
  FullyConstrained = true
  MakeInternals = false
  MapMode = 5
  Placement = pos=(0,0,0) rot=(1,0,0;3.14159rad)
  expr: Constraints[5] = VarSet.WallThickness + VarSet.Clearance
  expr: Constraints[6] = VarSet.WallThickness + VarSet.Clearance
  sketch-geometry (8):
    g0: LineSegment StartX=-12.1 StartY=-6.325 StartZ=0 EndX=-12.1 EndY=-18.325 EndZ=0
    g1: LineSegment StartX=-9.42 StartY=-18.325 StartZ=0 EndX=-9.42 EndY=-6.325 EndZ=0
    g2: LineSegment StartX=-9.42 StartY=19.055 StartZ=0 EndX=-9.42 EndY=7.055 EndZ=0
    g3: LineSegment StartX=-12.1 StartY=7.055 StartZ=0 EndX=-12.1 EndY=19.055 EndZ=0
    g4: LineSegment StartX=-12.1 StartY=-6.325 StartZ=0 EndX=-9.42 EndY=-6.325 EndZ=0
    g5: LineSegment StartX=-12.1 StartY=19.055 StartZ=0 EndX=-9.42 EndY=19.055 EndZ=0
    g6: LineSegment StartX=-9.42 StartY=7.055 StartZ=0 EndX=-12.1 EndY=7.055 EndZ=0
    g7: LineSegment StartX=-12.1 StartY=-18.325 StartZ=0 EndX=-9.42 EndY=-18.325 EndZ=0
  constraints (24):
    c: Vertical(g0)
    c: Vertical(g1)
    c: Vertical(g2)
    c: Vertical(g3)
    c: Vertical(g3,g0)
    c: DistanceX(g-5,g0) = 1.32
    c: DistanceY(g3,g-6) = 1.32
    c: Coincident(g4,g0)
    c: Coincident(g4,g1)
    c: Horizontal(g4)
    c: Coincident(g5,g3)
    c: Coincident(g5,g2)
    c: Horizontal(g5)
    c: Coincident(g6,g2)
    c: Coincident(g6,g3)
    c: Horizontal(g6)
    c: Vertical(g2,g1)
    c: Horizontal(g1,g-4)
    c: PointOnObject(g1,g-4)
    c: Coincident(g7,g0)
    c: Coincident(g7,g1)
    c: Horizontal(g7)
    c: DistanceY(g2,g2) = 12
    c: Equal(g2,g1)
FEATURE [PartDesign::Pad] Pad008  label="Holder001"
  BaseFeature = -> Pad007
  Direction = (0,0,-1)
  Length = 4.3
  Length2 = 10
  Profile = -> Sketch023
  ReferenceAxis = -> Sketch023 [N_Axis]
  Refine = true
  Suppressed = false
  Type = 0
FEATURE [Sketcher::SketchObject] Sketch024
  ArcFitTolerance = 1e-06
  AttachmentSupport = -> [Pad008]
  ExternalGeometry = -> [Pad008]
  ExternalTypes = [0,0]
  FullyConstrained = true
  MakeInternals = false
  MapMode = 5
  Placement = pos=(0,-19.055,0) rot=(1,0,0;1.5708rad)
  expr: Constraints[0] = 1 mm + 2 * VarSet.Clearance
  expr: Constraints[1] = 1.3 mm - VarSet.Clearance
  sketch-geometry (1):
    g0: Circle CenterX=-10.82 CenterY=-3 CenterZ=0 NormalX=0 NormalY=0 NormalZ=1 AngleXU=0 Radius=0.52
  constraints (3):
    c: Diameter(g0) = 1.04
    c: DistanceX(g-4,g0) = 1.28
    c: DistanceY(g0,g-3) = 3
FEATURE [Sketcher::SketchObject] Sketch024_Teardrops
  ArcFitTolerance = 1e-06
  AttachmentSupport = -> [Sketch024]
  ExternalTypes = [0]
  FullyConstrained = true
  MakeInternals = false
  MapMode = 2
  Placement = pos=(0,-19.055,0) rot=(1,0,0;1.5708rad)
  expr: Constraints[5] = Sketch024.Geometry[0].Center.x * 1 mm
  expr: Constraints[6] = Sketch024.Geometry[0].Center.y * 1 mm
  expr: Constraints[7] = Hole003.Diameter
  expr: Constraints[8] = Hole003.TeardropAngle
  expr: Constraints[9] = Hole003.TeardropRotation
  sketch-geometry (4):
    g0: ArcOfCircle CenterX=-10.82 CenterY=-3 CenterZ=0 NormalX=0 NormalY=0 NormalZ=1 AngleXU=0 Radius=0.52 StartAngle=5.23599 EndAngle=10.472
    g1: LineSegment StartX=-10.56 StartY=-3.45033 StartZ=0 EndX=-10.82 EndY=-3.60044 EndZ=0
    g2: LineSegment StartX=-11.08 StartY=-3.45033 StartZ=0 EndX=-10.82 EndY=-3.60044 EndZ=0
    g3: LineSegment [constr] StartX=-10.82 StartY=-3 StartZ=0 EndX=-10.82 EndY=-3.60044 EndZ=0
  constraints (10):
    c: Coincident(g1,g2)
    c: Coincident(g1,g3)
    c: Coincident(g0,g3)
    c: Tangent(g0,g1) = 1.5708
    c: Tangent(g0,g2) = -1.5708
    c: DistanceX(g0) = -10.82
    c: DistanceY(g0) = -3
    c: Diameter(g0) = 1.04
    c: Angle(g1,g2) = 2.0944
    c: Angle(g3) = 4.71239
FEATURE [App::Point] Origin012
  Role = Origin
FEATURE [Sketcher::SketchObject] Sketch025
  ArcFitTolerance = 1e-06
  AttachmentSupport = -> [Origin011]
  ExternalTypes = [0]
  FullyConstrained = false
  MakeInternals = false
  MapMode = 5
  Placement = pos=(0,0,0) rot=(1,0,0;1.5708rad)
  sketch-geometry (1):
    g0: Circle CenterX=-10.8237 CenterY=-1.70197 CenterZ=0 NormalX=0 NormalY=0 NormalZ=1 AngleXU=0 Radius=0.5
  constraints (1):
    c: Diameter(g0) = 1
FEATURE [PartDesign::Pad] Pad009
  Direction = (0,-1,0)
  Length = 55
  Length2 = 10
  Midplane = true
  Profile = -> Sketch025
  ReferenceAxis = -> Sketch025 [N_Axis]
  Refine = true
  Suppressed = false
  Type = 0
FEATURE [PartDesign::Body] Body005  label="Pin"
  AllowCompound = false
  Group = -> [Sketch025,Pad009]
  Origin = -> Origin011
  Tip = -> Pad009
FEATURE [Sketcher::SketchObject] Sketch028
  ArcFitTolerance = 1e-06
  AttachmentSupport = -> [Pad006]
  ExternalGeometry = -> [Pad006]
  ExternalTypes = [0,0]
  FullyConstrained = false
  MakeInternals = false
  MapMode = 5
  Placement = pos=(-6.95,0,0) rot=(0.57735,-0.57735,-0.57735;2.0944rad)
  sketch-geometry (3):
    g0: LineSegment StartX=14.5866 StartY=3.3 StartZ=0 EndX=13.055 EndY=1.76844 EndZ=0
    g1: LineSegment StartX=13.055 StartY=3.3 StartZ=0 EndX=14.5866 EndY=3.3 EndZ=0
    g2: LineSegment StartX=13.055 StartY=3.3 StartZ=0 EndX=13.055 EndY=1.76844 EndZ=0
  constraints (7):
    c: PointOnObject(g0,g-3)
    c: PointOnObject(g0,g-4)
    c: Coincident(g1,g-4)
    c: Coincident(g1,g0)
    c: Coincident(g2,g1)
    c: Coincident(g2,g0)
    c: Angle(g0,g2) = 0.785398
FEATURE [PartDesign::Pocket] Pocket011  label="Reset Button Print relief"
  BaseFeature = -> Pad006
  Direction = (1,0,0)
  Length = 5
  Length2 = 5
  Profile = -> Sketch028
  ReferenceAxis = -> Sketch028 [N_Axis]
  Refine = true
  Suppressed = false
  Type = 2
FEATURE [App::Point] Origin014
  Role = Origin
FEATURE [Sketcher::SketchObject] Sketch029
  ArcFitTolerance = 1e-06
  AttachmentSupport = -> [Origin013]
  ExternalTypes = [0]
  FullyConstrained = false
  MakeInternals = false
  MapMode = 5
  Placement = pos=(0,0,0) rot=(1,0,0;1.5708rad)
  sketch-geometry (1):
    g0: Circle CenterX=5.9348 CenterY=-2.47832 CenterZ=0 NormalX=0 NormalY=0 NormalZ=1 AngleXU=0 Radius=0.875
  constraints (1):
    c: Diameter(g0) = 1.75
FEATURE [PartDesign::Pad] Pad010
  Direction = (0,-1,0)
  Length = 3
  Length2 = 10
  Profile = -> Sketch029
  ReferenceAxis = -> Sketch029 [N_Axis]
  Refine = true
  Suppressed = false
  Type = 0
FEATURE [PartDesign::Body] Body006  label="Filament"
  AllowCompound = false
  Group = -> [Sketch029,Pad010]
  Origin = -> Origin013
  Placement = pos=(0,-17.2,0) rot=(0,0,1;0rad)
  Tip = -> Pad010
FEATURE [Sketcher::SketchObject] Sketch030
  ArcFitTolerance = 1e-06
  AttachmentSupport = -> [Hole_Teardrops]
  ExternalGeometry = -> [Hole]
  ExternalTypes = [0]
  FullyConstrained = true
  MakeInternals = false
  MapMode = 5
  Placement = pos=(0,20.375,-1.2e-14) rot=(0,0.707107,0.707107;3.14159rad)
  sketch-geometry (4):
    g0: LineSegment StartX=-5.82001 StartY=-1.18 StartZ=0 EndX=-10.82 EndY=-1.18 EndZ=0
    g1: LineSegment StartX=-5.82001 StartY=-2.22 StartZ=0 EndX=-10.82 EndY=-2.22 EndZ=0
    g2: ArcOfCircle CenterX=-5.82001 CenterY=-1.7 CenterZ=0 NormalX=0 NormalY=0 NormalZ=1 AngleXU=0 Radius=0.52 StartAngle=4.71239 EndAngle=7.85398
    g3: ArcOfCircle CenterX=-10.82 CenterY=-1.7 CenterZ=0 NormalX=0 NormalY=0 NormalZ=1 AngleXU=0 Radius=0.52 StartAngle=1.57081 EndAngle=4.71239
  constraints (10):
    c: Tangent(g0,g2) = -1.5708
    c: Tangent(g1,g2) = 1.5708
    c: Coincident(g3,g-3)
    c: PointOnObject(g3,g-3)
    c: Coincident(g0,g3)
    c: Tangent(g-3,g0)
    c: Tangent(g1,g3) = 1.5708
    c: Horizontal(g0)
    c: Horizontal(g1)
    c: DistanceX(g0,g0) = 5
FEATURE [PartDesign::Pocket] Pocket012  label="PinPocket"
  BaseFeature = -> Hole_Teardrops
  Direction = (0,-1,2e-16)
  Length = 0.5
  Length2 = 5
  Profile = -> Sketch030
  ReferenceAxis = -> Sketch030 [N_Axis]
  Refine = true
  Suppressed = false
  Type = 0
FEATURE [PartDesign::Mirrored] Mirrored001  label="PinMirror"
  BaseFeature = -> Pocket012
  MirrorPlane = -> Sketch010_Teardrops [V_Axis]
  Originals = -> [Hole_Teardrops,Pocket012]
  Refine = true
  Suppressed = false
  TransformMode = 0
FEATURE [Sketcher::SketchObject] Sketch026
  ArcFitTolerance = 1e-06
  AttachmentSupport = -> [Mirrored001]
  ExternalGeometry = -> [Mirrored001]
  ExternalTypes = [0]
  FullyConstrained = true
  MakeInternals = false
  MapMode = 5
  Placement = pos=(0,0,0) rot=(1,0,0;3.14159rad)
  expr: Constraints[18] = VarSet.ChocHoleWidth / 2 + VarSet.KeycapHorizontalClearance - VarSet.Clearance
  expr: Constraints[19] = 12 mm + 2 * VarSet.Clearance
  expr: Constraints[22] = 13.38 mm - 2 * VarSet.Clearance
  sketch-geometry (8):
    g0: LineSegment StartX=-9.4 StartY=7.035 StartZ=0 EndX=-9.4 EndY=19.075 EndZ=0
    g1: LineSegment StartX=-9.4 StartY=19.075 StartZ=0 EndX=-12.12 EndY=19.075 EndZ=0
    g2: LineSegment StartX=-12.12 StartY=19.075 StartZ=0 EndX=-12.12 EndY=7.035 EndZ=0
    g3: LineSegment StartX=-12.12 StartY=7.035 StartZ=0 EndX=-9.4 EndY=7.035 EndZ=0
    g4: LineSegment StartX=-12.12 StartY=-6.305 StartZ=0 EndX=-12.12 EndY=-18.345 EndZ=0
    g5: LineSegment StartX=-12.12 StartY=-18.345 StartZ=0 EndX=-9.4 EndY=-18.345 EndZ=0
    g6: LineSegment StartX=-9.4 StartY=-18.345 StartZ=0 EndX=-9.4 EndY=-6.305 EndZ=0
    g7: LineSegment StartX=-9.4 StartY=-6.305 StartZ=0 EndX=-12.12 EndY=-6.305 EndZ=0
  constraints (23):
    c: Coincident(g0,g1)
    c: Coincident(g1,g2)
    c: Coincident(g2,g3)
    c: Coincident(g3,g0)
    c: Vertical(g0)
    c: Vertical(g2)
    c: Horizontal(g1)
    c: Horizontal(g3)
    c: Coincident(g4,g5)
    c: Coincident(g5,g6)
    c: Coincident(g6,g7)
    c: Coincident(g7,g4)
    c: Vertical(g4)
    c: Vertical(g6)
    c: Horizontal(g5)
    c: Horizontal(g7)
    c: Coincident(g1,g-3)
    c: Vertical(g0,g6)
    c: DistanceX(g6,g-1) = 9.4
    c: DistanceY(g0,g0) = 12.04
    c: Equal(g6,g0)
    c: PointOnObject(g4,g-3)
    c: DistanceY(g6,g0) = 13.34
FEATURE [PartDesign::Pocket] Pocket009  label="HolderHole"
  BaseFeature = -> Mirrored001
  Direction = (0,0,1)
  Length = 5
  Length2 = 5
  Profile = -> Sketch026
  ReferenceAxis = -> Sketch026 [N_Axis]
  Refine = true
  Suppressed = false
  Type = 1
FEATURE [PartDesign::Mirrored] Mirrored003  label="HolderHoleMirror"
  BaseFeature = -> Pocket009
  MirrorPlane = -> Sketch026 [V_Axis]
  Originals = -> [Pocket009]
  Refine = true
  Suppressed = false
  TransformMode = 0
FEATURE [Sketcher::SketchObject] Sketch027
  ArcFitTolerance = 1e-06
  AttachmentSupport = -> [Mirrored003]
  ExternalGeometry = -> [Hole_Teardrops]
  ExternalTypes = [0,0,0,0]
  FullyConstrained = true
  MakeInternals = false
  MapMode = 5
  Placement = pos=(0,-19.075,0) rot=(0,0.707107,0.707107;3.14159rad)
FEATURE [PartDesign::Pocket] Pocket010  label="PinPocket2"
  BaseFeature = -> Mirrored003
  Direction = (0,-1,2e-16)
  Length = 0.65
  Length2 = 5
  Profile = -> Sketch027
  ReferenceAxis = -> Sketch027 [N_Axis]
  Refine = true
  Suppressed = false
  Type = 0
  expr: Length = VarSet.WallThickness / 2
FEATURE [PartDesign::Mirrored] Mirrored004
  BaseFeature = -> Pocket010
  MirrorPlane = -> Sketch027 [V_Axis]
  Originals = -> [Pocket010]
  Refine = true
  Suppressed = false
  TransformMode = 0
FEATURE [PartDesign::Chamfer] Chamfer  label="HoldChamfer"
  Angle = 45
  Base = -> Pad008 [Edge40,Edge52]
  BaseFeature = -> Pad008
  ChamferType = 0
  FlipDirection = false
  Refine = true
  Size = 3
  Size2 = 1
  SupportTransform = false
  Suppressed = false
  UseAllEdges = false
FEATURE [PartDesign::Hole] Hole003  label="PinHole002"
  BaseFeature = -> Chamfer
  BaseProfileType = 7
  CustomThreadClearance = 0
  Depth = 102.162
  DepthType = 1
  Diameter = 1.04
  DrillForDepth = false
  DrillPoint = 1
  DrillPointAngle = 118
  HoleCutCountersinkAngle = 90
  HoleCutCustomValues = false
  HoleCutDepth = 0
  HoleCutDiameter = 0
  HoleCutType = 0
  ModelThread = false
  Profile = -> Sketch024
  Refine = true
  Suppressed = false
  Tapered = false
  TaperedAngle = 90
  TeardropAngle = 120
  TeardropRotation = 270
  ThreadClass = 0
  ThreadDepth = 102.162
  ThreadDepthType = 0
  ThreadDiameter = 1.04
  ThreadDirection = 0
  ThreadFit = 0
  ThreadSize = 0
  ThreadType = 0
  Threaded = false
  UseCustomThreadClearance = false
  expr: Diameter = 1 mm + 2 * VarSet.Clearance
FEATURE [PartDesign::Pocket] Hole003_Teardrops  label="PinHole_Teardrops002"
  BaseFeature = -> Hole003
  Direction = (0,1,-2e-16)
  Length = 102.162
  Length2 = 5
  Profile = -> Sketch024_Teardrops
  ReferenceAxis = -> Sketch024_Teardrops [N_Axis]
  Refine = true
  Suppressed = false
  Type = 1
  expr: Length = Hole003.Depth
  expr: Type = Hole003.DepthType
FEATURE [PartDesign::Mirrored] Mirrored  label="PinholeMirror"
  BaseFeature = -> Hole003_Teardrops
  MirrorPlane = -> Sketch023 [V_Axis]
  Originals = -> [Pad008,Hole003,Hole003_Teardrops,Chamfer]
  Refine = true
  Suppressed = false
  TransformMode = 0
FEATURE [Sketcher::SketchObject] Sketch031
  ArcFitTolerance = 1e-06
  AttachmentSupport = -> [Mirrored]
  ExternalGeometry = -> [Mirrored]
  ExternalTypes = [0,0,0]
  FullyConstrained = false
  MakeInternals = false
  MapMode = 5
  Placement = pos=(0,0,0) rot=(1,0,0;3.14159rad)
  sketch-geometry (5):
    g0: ArcOfCircle CenterX=0 CenterY=10.084 CenterZ=0 NormalX=0 NormalY=0 NormalZ=1 AngleXU=0 Radius=8.135 StartAngle=5.23599 EndAngle=10.472
    g1: LineSegment [constr] StartX=-9.42 StartY=19.055 StartZ=0 EndX=0 EndY=10.084 EndZ=0
    g2: LineSegment [constr] StartX=9.42 StartY=19.055 StartZ=0 EndX=0 EndY=10.084 EndZ=0
    g3: LineSegment StartX=0 StartY=0.690511 StartZ=0 EndX=4.0675 EndY=3.03888 EndZ=0
    g4: LineSegment StartX=0 StartY=0.690511 StartZ=0 EndX=-4.0675 EndY=3.03888 EndZ=0
  constraints (11):
    c: Coincident(g1,g-3)
    c: Coincident(g1,g0)
    c: Coincident(g2,g-4)
    c: Coincident(g2,g0)
    c: Equal(g1,g2)
    c: PointOnObject(g3,g-2)
    c: Coincident(g4,g3)
    c: Angle(g3,g4) = 2.0944
    c: Diameter(g0) = 16.27
    c: Tangent(g3,g0) = -1.5708
    c: Tangent(g4,g0) = 1.5708
FEATURE [PartDesign::Pocket] Pocket013  label="3Muenzhalter"
  BaseFeature = -> Mirrored
  Direction = (0,0,1)
  Length = 5.07
  Length2 = 5
  Profile = -> Sketch031
  ReferenceAxis = -> Sketch031 [N_Axis]
  Refine = true
  Suppressed = false
  Type = 0
  expr: Length = 3 * (1.67 mm + VarSet.Clearance)
FEATURE [Sketcher::SketchObject] Sketch032
  ArcFitTolerance = 1e-06
  AttachmentSupport = -> [Pocket013]
  ExternalGeometry = -> [Pocket013]
  ExternalTypes = [0,0,0]
  FullyConstrained = true
  MakeInternals = false
  MapMode = 5
  Placement = pos=(0,-20.375,0) rot=(1,0,0;1.5708rad)
  sketch-geometry (20):
    g0: ArcOfCircle CenterX=-16.9417 CenterY=12.5217 CenterZ=0 NormalX=0 NormalY=0 NormalZ=1 AngleXU=0 Radius=5 StartAngle=5.59694 EndAngle=11.6818
    g1: LineSegment StartX=-12.72 StartY=9 StartZ=0 EndX=-13.0736 EndY=9.35355 EndZ=0
    g2: LineSegment StartX=-13.42 StartY=8.3 StartZ=0 EndX=-13.7736 EndY=8.65355 EndZ=0
    g3: LineSegment StartX=-13.42 StartY=9 StartZ=0 EndX=-13.42 EndY=8.3 EndZ=0
    g4: LineSegment StartX=-13.42 StartY=9 StartZ=0 EndX=-12.72 EndY=9 EndZ=0
    g5: ArcOfCircle CenterX=-16.9417 CenterY=-3.52172 CenterZ=0 NormalX=0 NormalY=0 NormalZ=1 AngleXU=0 Radius=5 StartAngle=0.884556 EndAngle=6.96943
    g6: LineSegment StartX=-12.72 StartY=0 StartZ=0 EndX=-13.0736 EndY=-0.353553 EndZ=0
    g7: LineSegment StartX=-12.72 StartY=0 StartZ=0 EndX=-13.42 EndY=0 EndZ=0
    g8: LineSegment StartX=-13.42 StartY=0.7 StartZ=0 EndX=-13.7736 EndY=0.346447 EndZ=0
    g9: LineSegment StartX=-13.42 StartY=0.7 StartZ=0 EndX=-13.42 EndY=0 EndZ=0
    g10: ArcOfCircle CenterX=16.9417 CenterY=12.5217 CenterZ=0 NormalX=0 NormalY=0 NormalZ=1 AngleXU=0 Radius=5 StartAngle=4.02615 EndAngle=10.111
    g11: ArcOfCircle CenterX=16.9417 CenterY=-3.52172 CenterZ=0 NormalX=0 NormalY=0 NormalZ=1 AngleXU=0 Radius=5 StartAngle=2.45535 EndAngle=8.54022
    g12: LineSegment StartX=13.0736 StartY=9.35355 StartZ=0 EndX=12.72 EndY=9 EndZ=0
    g13: LineSegment StartX=12.72 StartY=9 StartZ=0 EndX=13.42 EndY=9 EndZ=0
    g14: LineSegment StartX=13.42 StartY=9 StartZ=0 EndX=13.42 EndY=8.3 EndZ=0
    g15: LineSegment StartX=13.42 StartY=8.3 StartZ=0 EndX=13.7736 EndY=8.65355 EndZ=0
    g16: LineSegment StartX=13.7736 StartY=0.346447 StartZ=0 EndX=13.42 EndY=0.7 EndZ=0
    g17: LineSegment StartX=13.42 StartY=0.7 StartZ=0 EndX=13.42 EndY=0 EndZ=0
    g18: LineSegment StartX=13.42 StartY=0 StartZ=0 EndX=12.72 EndY=0 EndZ=0
    g19: LineSegment StartX=12.72 StartY=0 StartZ=0 EndX=13.0736 EndY=-0.353553 EndZ=0
  constraints (60):
    c: PointOnObject(g1,g-3)
    c: PointOnObject(g2,g-4)
    c: Parallel(g1,g2)
    c: Angle(g1,g-3) = 0.785398
    c: Coincident(g3,g-4)
    c: Coincident(g3,g2)
    c: Coincident(g4,g3)
    c: Coincident(g4,g1)
    c: Equal(g4,g3)
    c: Equal(g2,g1)
    c: Coincident(g1,g0)
    c: Coincident(g2,g0)
    c: Distance(g1,g1) = 0.5
    c: Radius(g0) = 5
    c: PointOnObject(g6,g-1)
    c: Coincident(g7,g6)
    c: Coincident(g7,g-4)
    c: PointOnObject(g8,g-4)
    c: Coincident(g9,g8)
    c: Coincident(g9,g7)
    c: Parallel(g6,g8)
    c: Equal(g8,g6)
    c: Angle(g8,g9) = 0.785398
    c: Equal(g5,g0)
    c: Coincident(g6,g5)
    c: Coincident(g8,g5)
    c: Equal(g7,g9)
    c: PointOnObject(g12,g-3)
    c: Coincident(g12,g13)
    c: Coincident(g13,g-5)
    c: Coincident(g13,g14)
    c: PointOnObject(g14,g-5)
    c: Coincident(g14,g15)
    c: PointOnObject(g16,g-5)
    c: Coincident(g16,g17)
    c: Coincident(g17,g-5)
    c: Coincident(g17,g18)
    c: PointOnObject(g18,g-1)
    c: Coincident(g18,g19)
    c: Parallel(g15,g12)
    c: Parallel(g16,g19)
    c: Equal(g15,g12)
    c: Equal(g13,g14)
    c: Equal(g16,g19)
    c: Equal(g18,g17)
    c: Angle(g15,g14) = 0.785398
    c: Angle(g17,g16) = 0.785398
    c: Equal(g12,g1)
    c: Equal(g16,g15)
    c: Coincident(g15,g10)
    c: Equal(g0,g10)
    c: Coincident(g12,g10)
    c: Coincident(g19,g11)
    c: Coincident(g16,g11)
    c: Equal(g10,g11)
    c: Equal(g17,g14)
    c: Equal(g14,g4)
    c: Equal(g4,g7)
    c: Equal(g8,g1)
    c: Distance(g4,g4) = 0.7
FEATURE [PartDesign::Pad] Pad011  label="MouseEars"
  BaseFeature = -> Pocket013
  Direction = (0,-1,2e-16)
  Length = 0.2
  Length2 = 10
  Profile = -> Sketch032
  ReferenceAxis = -> Sketch032 [N_Axis]
  Refine = true
  Reversed = true
  Suppressed = false
  Type = 0
FEATURE [Sketcher::SketchObject] Sketch033
  ArcFitTolerance = 1e-06
  AttachmentSupport = -> [Pad011]
  ExternalTypes = [0]
  FullyConstrained = false
  MakeInternals = false
  MapMode = 5
  Placement = pos=(0,0,9) rot=(0,0,1;0rad)
  sketch-geometry (12):
    g0: LineSegment [constr] StartX=5.1026 StartY=-4.22004 StartZ=0 EndX=0 EndY=-13.058 EndZ=0
    g1: LineSegment [constr] StartX=0 StartY=-13.058 StartZ=0 EndX=-5.1026 EndY=-4.22004 EndZ=0
    g2: LineSegment [constr] StartX=-5.1026 StartY=-4.22004 StartZ=0 EndX=5.1026 EndY=-4.22004 EndZ=0
    g3: ArcOfCircle CenterX=-5.96863 CenterY=-3.72004 CenterZ=0 NormalX=0 NormalY=0 NormalZ=1 AngleXU=0 Radius=4 StartAngle=6.15786 EndAngle=11.6445
    g4: ArcOfCircle CenterX=5.96863 CenterY=-3.72004 CenterZ=0 NormalX=0 NormalY=0 NormalZ=1 AngleXU=0 Radius=4 StartAngle=4.06346 EndAngle=9.55011
    g5: ArcOfCircle CenterX=5e-16 CenterY=-14.058 CenterZ=0 NormalX=0 NormalY=0 NormalZ=1 AngleXU=0 Radius=4 StartAngle=1.96907 EndAngle=7.45571
    g6: LineSegment StartX=1.5513 StartY=-10.3711 StartZ=0 EndX=0 EndY=-13.058 EndZ=0
    g7: LineSegment StartX=-1.5513 StartY=-10.3711 StartZ=0 EndX=0 EndY=-13.058 EndZ=0
    g8: LineSegment StartX=-3.5513 StartY=-6.90697 StartZ=0 EndX=-5.1026 EndY=-4.22004 EndZ=0
    g9: LineSegment StartX=-2 StartY=-4.22004 StartZ=0 EndX=-5.1026 EndY=-4.22004 EndZ=0
    g10: LineSegment StartX=2 StartY=-4.22004 StartZ=0 EndX=5.1026 EndY=-4.22004 EndZ=0
    g11: LineSegment StartX=5.1026 StartY=-4.22004 StartZ=0 EndX=3.5513 EndY=-6.90697 EndZ=0
  constraints (35):
    c: PointOnObject(g0,g-2)
    c: Coincident(g1,g0)
    c: Coincident(g2,g1)
    c: Coincident(g2,g0)
    c: Horizontal(g2)
    c: Equal(g1,g2)
    c: Equal(g2,g0)
    c: PointOnObject(g3,g1)
    c: PointOnObject(g3,g2)
    c: PointOnObject(g4,g2)
    c: PointOnObject(g4,g0)
    c: PointOnObject(g5,g1)
    c: PointOnObject(g5,g0)
    c: Coincident(g6,g5)
    c: Coincident(g6,g0)
    c: Coincident(g7,g5)
    c: Coincident(g7,g0)
    c: Coincident(g8,g3)
    c: Coincident(g8,g1)
    c: Coincident(g9,g3)
    c: Coincident(g9,g1)
    c: Coincident(g10,g4)
    c: Coincident(g10,g0)
    c: Coincident(g11,g0)
    c: Coincident(g11,g4)
    c: Equal(g5,g3)
    c: Equal(g3,g4)
    c: Radius(g3) = 4
    c: Equal(g11,g6)
    c: Equal(g6,g7)
    c: Equal(g7,g8)
    c: Equal(g8,g9)
    c: Equal(g9,g10)
    c: Distance(g0,g4) = 1
    c: Distance(g3,g5) = 4
FEATURE [PartDesign::Pocket] Pocket014  label="Symbol"
  BaseFeature = -> Pad011
  Direction = (0,0,-1)
  Length = 0.5
  Length2 = 5
  Profile = -> Sketch033
  ReferenceAxis = -> Sketch033 [N_Axis]
  Refine = true
  Suppressed = false
  Type = 0
FEATURE [PartDesign::Body] Body004  label="Keywell"
  AllowCompound = false
  Group = -> [Sketch022,Pad007,Sketch023,Pad008,Chamfer,Sketch024,Hole003,Sketch024_Teardrops,Hole003_Teardrops,Mirrored,Sketch031,Pocket013,Sketch032,Pad011,Sketch033,Pocket014]
  Origin = -> Origin009
  Placement = pos=(0,0,1.3) rot=(0,0,1;0rad)
  Tip = -> Pocket014
  expr: .Placement.Base.z = VarSet.WallThickness
FEATURE [Sketcher::SketchObject] Sketch034
  ArcFitTolerance = 1e-06
  AttachmentOffset = pos=(0,0,-1.3) rot=(0,0,1;0rad)
  AttachmentSupport = -> [Mirrored001]
  ExternalGeometry = -> [Mirrored001]
  ExternalTypes = [0,0,0,0]
  FullyConstrained = true
  MakeInternals = false
  MapMode = 5
  Placement = pos=(0,0,1.3) rot=(1,0,0;3.14159rad)
  expr: .AttachmentOffset.Base.z = -VarSet.WallThickness
  sketch-geometry (20):
    g0: ArcOfCircle CenterX=16.9197 CenterY=23.8747 CenterZ=0 NormalX=0 NormalY=0 NormalZ=1 AngleXU=0 Radius=5 StartAngle=4.03183 EndAngle=10.1053
    g1: ArcOfCircle CenterX=16.9197 CenterY=-23.8747 CenterZ=0 NormalX=0 NormalY=0 NormalZ=1 AngleXU=0 Radius=5 StartAngle=2.46104 EndAngle=8.53454
    g2: ArcOfCircle CenterX=-16.9197 CenterY=-23.8747 CenterZ=0 NormalX=0 NormalY=0 NormalZ=1 AngleXU=0 Radius=5 StartAngle=0.890242 EndAngle=6.96374
    g3: ArcOfCircle CenterX=-16.9197 CenterY=23.8747 CenterZ=0 NormalX=0 NormalY=0 NormalZ=1 AngleXU=0 Radius=5 StartAngle=5.60263 EndAngle=11.6761
    g4: LineSegment StartX=-13.0336 StartY=20.7286 StartZ=0 EndX=-12.68 EndY=20.375 EndZ=0
    g5: LineSegment StartX=-12.68 StartY=20.375 StartZ=0 EndX=-13.42 EndY=20.375 EndZ=0
    g6: LineSegment StartX=-13.42 StartY=20.375 StartZ=0 EndX=-13.42 EndY=19.635 EndZ=0
    g7: LineSegment StartX=-13.42 StartY=19.635 StartZ=0 EndX=-13.7736 EndY=19.9886 EndZ=0
    g8: LineSegment StartX=13.0336 StartY=20.7286 StartZ=0 EndX=12.68 EndY=20.375 EndZ=0
    g9: LineSegment StartX=12.68 StartY=20.375 StartZ=0 EndX=13.42 EndY=20.375 EndZ=0
    g10: LineSegment StartX=13.42 StartY=20.375 StartZ=0 EndX=13.42 EndY=19.635 EndZ=0
    g11: LineSegment StartX=13.42 StartY=19.635 StartZ=0 EndX=13.7736 EndY=19.9886 EndZ=0
    g12: LineSegment StartX=13.7736 StartY=-19.9886 StartZ=0 EndX=13.42 EndY=-19.635 EndZ=0
    g13: LineSegment StartX=13.42 StartY=-19.635 StartZ=0 EndX=13.42 EndY=-20.375 EndZ=0
    g14: LineSegment StartX=13.42 StartY=-20.375 StartZ=0 EndX=12.68 EndY=-20.375 EndZ=0
    g15: LineSegment StartX=12.68 StartY=-20.375 StartZ=0 EndX=13.0336 EndY=-20.7286 EndZ=0
    g16: LineSegment StartX=-13.0336 StartY=-20.7286 StartZ=0 EndX=-12.68 EndY=-20.375 EndZ=0
    g17: LineSegment StartX=-12.68 StartY=-20.375 StartZ=0 EndX=-13.42 EndY=-20.375 EndZ=0
    g18: LineSegment StartX=-13.42 StartY=-20.375 StartZ=0 EndX=-13.42 EndY=-19.635 EndZ=0
    g19: LineSegment StartX=-13.42 StartY=-19.635 StartZ=0 EndX=-13.7736 EndY=-19.9886 EndZ=0
  constraints (60):
    c: PointOnObject(g4,g-3)
    c: Coincident(g4,g5)
    c: Coincident(g5,g-6)
    c: Coincident(g5,g6)
    c: PointOnObject(g6,g-6)
    c: Coincident(g6,g7)
    c: PointOnObject(g8,g-3)
    c: Coincident(g8,g9)
    c: Coincident(g9,g-4)
    c: Coincident(g9,g10)
    c: PointOnObject(g10,g-4)
    c: Coincident(g10,g11)
    c: PointOnObject(g12,g-4)
    c: Coincident(g12,g13)
    c: Coincident(g13,g-5)
    c: Coincident(g13,g14)
    c: PointOnObject(g14,g-5)
    c: Coincident(g14,g15)
    c: PointOnObject(g16,g-5)
    c: Coincident(g16,g17)
    c: Coincident(g17,g-6)
    c: Coincident(g17,g18)
    c: PointOnObject(g18,g-6)
    c: Coincident(g18,g19)
    c: Coincident(g16,g2)
    c: Coincident(g19,g2)
    c: Coincident(g12,g1)
    c: Coincident(g15,g1)
    c: Coincident(g8,g0)
    c: Coincident(g11,g0)
    c: Coincident(g4,g3)
    c: Coincident(g7,g3)
    c: Angle(g4,g5) = 0.785398
    c: Angle(g9,g8) = 0.785398
    c: Angle(g13,g12) = 0.785398
    c: Angle(g19,g18) = 0.785398
    c: Parallel(g16,g19)
    c: Parallel(g15,g12)
    c: Parallel(g11,g8)
    c: Parallel(g4,g7)
    c: Equal(g4,g8)
    c: Equal(g8,g7)
    c: Equal(g7,g19)
    c: Equal(g19,g16)
    c: Equal(g16,g15)
    c: Equal(g15,g12)
    c: Equal(g12,g11)
    c: Equal(g9,g10)
    c: Equal(g10,g5)
    c: Equal(g5,g6)
    c: Equal(g6,g13)
    c: Equal(g13,g14)
    c: Equal(g14,g18)
    c: Equal(g18,g17)
    c: Equal(g0,g3)
    c: Equal(g3,g1)
    c: Equal(g1,g2)
    c: Radius(g0) = 5
    c: Distance(g8,g8) = 0.5
    c: Distance(g9,g9) = 0.74
FEATURE [PartDesign::Pad] Pad012  label="MouseEars001"
  BaseFeature = -> Mirrored004
  Direction = (0,0,-1)
  Length = 0.2
  Length2 = 10
  Profile = -> Sketch034
  ReferenceAxis = -> Sketch034 [N_Axis]
  Refine = true
  Suppressed = false
  Type = 0
FEATURE [PartDesign::Body] Body
  AllowCompound = false
  Group = -> [Sketch,Pad,Sketch001,Pocket,Sketch002,Pad001,Sketch003,Pocket001,Sketch004,Pocket002,Sketch005,Pocket003,Sketch010,Hole,Sketch010_Teardrops,Hole_Teardrops,Pocket012,Mirrored001,Sketch026,Pocket009,Mirrored003,Sketch027,Pocket010,Mirrored004,Sketch030,Sketch034,Pad012]
  Origin = -> Origin
  Tip = -> Pad012
FEATURE [Sketcher::SketchObject] Sketch035
  ArcFitTolerance = 1e-06
  AttachmentSupport = -> [Pocket011]
  ExternalGeometry = -> [Pocket011]
  ExternalTypes = [0,0,0,0]
  FullyConstrained = false
  MakeInternals = false
  MapMode = 5
  Placement = pos=(0,19.055,0) rot=(0,0.707107,0.707107;3.14159rad)
  sketch-geometry (20):
    g0: LineSegment StartX=-7.5 StartY=1.3 StartZ=0 EndX=-7.5 EndY=3.3 EndZ=0
    g1: ArcOfCircle CenterX=-8 CenterY=3.3 CenterZ=0 NormalX=0 NormalY=0 NormalZ=1 AngleXU=0 Radius=0.5 StartAngle=1e-16 EndAngle=1.5708
    g2: LineSegment StartX=-8 StartY=3.8 StartZ=0 EndX=-13.6 EndY=3.8 EndZ=0
    g3: ArcOfCircle CenterX=-13.6 CenterY=3.3 CenterZ=0 NormalX=0 NormalY=0 NormalZ=1 AngleXU=0 Radius=0.5 StartAngle=1.5708 EndAngle=3.14159
    g4: LineSegment StartX=-14.1 StartY=3.3 StartZ=0 EndX=-14.1 EndY=-2 EndZ=0
    g5: ArcOfCircle CenterX=-13.6 CenterY=-2 CenterZ=0 NormalX=0 NormalY=0 NormalZ=1 AngleXU=0 Radius=0.5 StartAngle=3.14159 EndAngle=4.71239
    g6: LineSegment StartX=-13.6 StartY=-2.5 StartZ=0 EndX=-8 EndY=-2.5 EndZ=0
    g7: ArcOfCircle CenterX=-8 CenterY=-2 CenterZ=0 NormalX=0 NormalY=0 NormalZ=1 AngleXU=0 Radius=0.5 StartAngle=4.71239 EndAngle=6.28319
    g8: LineSegment StartX=-7.5 StartY=-2 StartZ=0 EndX=-7.5 EndY=0 EndZ=0
    g9: LineSegment StartX=-11.85 StartY=0 StartZ=0 EndX=-11.85 EndY=1.3 EndZ=0
    g10: LineSegment StartX=-11.85 StartY=1.3 StartZ=0 EndX=-11.3912 EndY=1.3 EndZ=0
    g11: LineSegment StartX=-11.85 StartY=0 StartZ=0 EndX=-11.3358 EndY=0 EndZ=0
    g12: LineSegment StartX=-7.84552 StartY=1.3 StartZ=0 EndX=-7.84552 EndY=1.58778 EndZ=0
    g13: LineSegment StartX=-7.84552 StartY=1.58778 StartZ=0 EndX=-11.3912 EndY=1.58778 EndZ=0
    g14: LineSegment StartX=-11.3912 StartY=1.58778 StartZ=0 EndX=-11.3912 EndY=1.3 EndZ=0
    g15: LineSegment StartX=-11.3358 StartY=0 StartZ=0 EndX=-11.3358 EndY=-0.305097 EndZ=0
    g16: LineSegment StartX=-11.3358 StartY=-0.305097 StartZ=0 EndX=-7.79473 EndY=-0.305097 EndZ=0
    g17: LineSegment StartX=-7.79473 StartY=-0.305097 StartZ=0 EndX=-7.79473 EndY=0 EndZ=0
    g18: LineSegment StartX=-7.84552 StartY=1.3 StartZ=0 EndX=-7.5 EndY=1.3 EndZ=0
    g19: LineSegment StartX=-7.79473 StartY=0 StartZ=0 EndX=-7.5 EndY=0 EndZ=0
  constraints (46):
    c: PointOnObject(g0,g-5)
    c: Vertical(g0)
    c: Tangent(g0,g1) = -1.5708
    c: Tangent(g1,g2) = -1.5708
    c: Tangent(g2,g3) = -1.5708
    c: Tangent(g3,g4) = -1.5708
    c: Tangent(g4,g5) = -1.5708
    c: Tangent(g5,g6) = -1.5708
    c: Tangent(g6,g7) = -1.5708
    c: Tangent(g7,g8) = -1.5708
    c: PointOnObject(g8,g-1)
    c: Vertical(g8)
    c: Horizontal(g6)
    c: Vertical(g4)
    c: Horizontal(g2)
    c: Equal(g1,g3)
    c: Equal(g3,g5)
    c: Equal(g5,g7)
    c: Equal(g2,g6)
    c: Equal(g0,g8)
    c: PointOnObject(g9,g-5)
    c: PointOnObject(g9,g-1)
    c: DistanceX(g-5,g9) = 0.25
    c: Vertical(g9,g9)
    c: Radius(g3) = 0.5
    c: DistanceX(g4,g-4) = 2
    c: DistanceY(g0,g0) = 2
    c: DistanceX(g-6,g0) = 2
    c: Coincident(g10,g9)
    c: Coincident(g18,g0)
    c: Coincident(g11,g9)
    c: Coincident(g19,g8)
    c: Coincident(g12,g13)
    c: Coincident(g13,g14)
    c: Horizontal(g13)
    c: Vertical(g12)
    c: Vertical(g14)
    c: Coincident(g15,g16)
    c: Coincident(g16,g17)
    c: Vertical(g15)
    c: Vertical(g17)
    c: Horizontal(g16)
    c: Coincident(g14,g10)
    c: Coincident(g18,g12)
    c: Coincident(g15,g11)
    c: Coincident(g19,g17)
FEATURE [PartDesign::Pad] Pad013  label="Brim"
  BaseFeature = -> Pocket011
  Direction = (0,1,-2e-16)
  Length = 0.2
  Length2 = 10
  Profile = -> Sketch035
  ReferenceAxis = -> Sketch035 [N_Axis]
  Refine = true
  Reversed = true
  Suppressed = false
  Type = 0
FEATURE [Sketcher::SketchObject] Sketch036
  ArcFitTolerance = 1e-06
  AttachmentSupport = -> [Pad013]
  ExternalGeometry = -> [Pad013]
  ExternalTypes = [0,0,0,0,0]
  FullyConstrained = false
  MakeInternals = false
  MapMode = 5
  Placement = pos=(0,18.855,0) rot=(1,0,0;1.5708rad)
  sketch-geometry (4):
    g0: LineSegment StartX=11.6717 StartY=-1e-16 StartZ=0 EndX=11.6717 EndY=-2.5 EndZ=0
    g1: LineSegment StartX=11.6717 StartY=-2.5 StartZ=0 EndX=12.0717 EndY=-2.5 EndZ=0
    g2: LineSegment StartX=12.0717 StartY=-2.5 StartZ=0 EndX=12.0717 EndY=0 EndZ=0
    g3: LineSegment StartX=11.6717 StartY=-1e-16 StartZ=0 EndX=12.0717 EndY=0 EndZ=0
  constraints (11):
    c: PointOnObject(g0,g-7)
    c: Vertical(g0)
    c: Coincident(g0,g1)
    c: PointOnObject(g1,g-7)
    c: Coincident(g1,g2)
    c: Vertical(g2)
    c: Equal(g0,g2)
    c: Distance(g1,g1) = 0.4
    c: Coincident(g3,g0)
    c: Coincident(g3,g2)
    c: PointOnObject(g2,g-4)
FEATURE [PartDesign::Pad] Pad014  label="Support"
  BaseFeature = -> Pad013
  Direction = (0,-1,2e-16)
  Length = 37
  Length2 = 10
  Profile = -> Sketch036
  ReferenceAxis = -> Sketch036 [N_Axis]
  Refine = true
  Suppressed = false
  Type = 0
FEATURE [Sketcher::SketchObject] Sketch037
  ArcFitTolerance = 1e-06
  AttachmentSupport = -> [Pad014]
  ExternalGeometry = -> [Pad014,Sketch036]
  ExternalTypes = [0,0]
  FullyConstrained = true
  MakeInternals = false
  MapMode = 5
  Placement = pos=(12.0717,0,0) rot=(0.57735,0.57735,0.57735;2.0944rad)
  sketch-geometry (2):
    g0: ArcOfCircle CenterX=-17.445 CenterY=0 CenterZ=0 NormalX=0 NormalY=0 NormalZ=1 AngleXU=0 Radius=0.5 StartAngle=3.14159 EndAngle=6.28319
    g1: LineSegment StartX=-17.945 StartY=1e-16 StartZ=0 EndX=-16.945 EndY=-1e-16 EndZ=0
  constraints (7):
    c: PointOnObject(g0,g-1)
    c: PointOnObject(g0,g-1)
    c: Radius(g0) = 0.5
    c: PointOnObject(g0,g-1)
    c: DistanceX(g-3,g0) = 0.2
    c: Coincident(g1,g0)
    c: Coincident(g1,g0)
FEATURE [PartDesign::Pocket] Pocket015  label="SupportRelief"
  BaseFeature = -> Pad014
  Direction = (-1,0,0)
  Length = 5
  Length2 = 5
  Profile = -> Sketch037
  ReferenceAxis = -> Sketch037 [N_Axis]
  Refine = true
  Suppressed = false
  Type = 2
FEATURE [PartDesign::LinearPattern] LinearPattern  label="LotsOfSupportRelief"
  BaseFeature = -> Pocket015
  Direction = -> Sketch037 [H_Axis]
  Length = 36
  Mode = 0
  Occurrences = 30
  Offset = 1.24138
  Originals = -> [Pocket015]
  Refine = true
  Suppressed = false
  TransformMode = 0
FEATURE [PartDesign::Body] Body003  label="Bottom"
  AllowCompound = false
  Group = -> [Sketch016,Pad004,Sketch017,Pocket007,Sketch018,Sketch019,Pad005,Sketch020,Hole002,Mirrored002,Pocket008,Sketch021,Pad006,Sketch028,Pocket011,Sketch035,Pad013,Sketch036,Pad014,Sketch037,Pocket015,LinearPattern]
  Origin = -> Origin007
  Placement = pos=(0,0,-4.4) rot=(0,0,1;0rad)
  Tip = -> LinearPattern
  expr: .Placement.Base.z = -(VarSet.ChocBottomClearance - VarSet.WallThickness)
